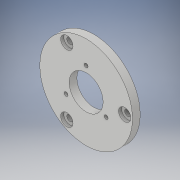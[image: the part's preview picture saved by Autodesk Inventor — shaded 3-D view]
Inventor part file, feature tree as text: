
AUTODESK INVENTOR PART (.ipt)
format: ipt  version: 2018 (Build 220112000, 112)  size: 143,872 bytes
history: native  units: in
note: dims shown in document units (in); Inventor stores cm internally (conversion verified against a paired STEP export)
features: extrude x8, sketch x4
ambient origin geometry x8: Origin, YZ Plane, XZ Plane, XY Plane, X Axis, Y Axis, Z Axis, Center Point
bodies: Solid1 (feature_tree)
feature tree (12):
  extrude  "Extrusion1"  Depth=2.3622in
  sketch  "Sketch2"  dims[d3=0.0984in d4=1.1811in d6=360.0deg]
  extrude  "Extrusion2"  Depth=1.1811in TaperAngle=360.0deg
  extrude  "Extrusion3"  Depth=0.1969in
  extrude  "Extrusion4"  Depth=0.0787in TaperAngle=0.0deg
  sketch  "Sketch3"  dims[d8=0.1969in d9=0.0in d12=0.315in]
  extrude  "Extrusion5"  Depth=0.0787in TaperAngle=0.0deg
  extrude  "Extrusion6"  Depth=0.0787in TaperAngle=0.0deg
  extrude  "Extrusion7"  Depth=0.1575in
  extrude  "Extrusion8"  Depth=1.1811in TaperAngle=360.0deg
  sketch  "Sketch1"  dims[d0=0.7874in d1=2.3622in]
  sketch  "Sketch4"  dims[d13=1.1811in d15=360.0deg d17=0.0787in d18=0.0in d19=0.0787in d20=0.0in d21=0.0787in d22=0.0in d23=0.1575in d24=1.1811in d26=360.0deg d28=0.0787in d29=0.0in d30=0.0787in d31=0.0in d32=0.0787in d33=0.0in d34=0.0394in d35=0.3937in d36=0.0in]
